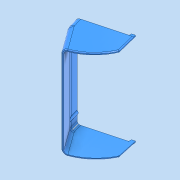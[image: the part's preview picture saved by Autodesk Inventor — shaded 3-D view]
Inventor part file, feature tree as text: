
AUTODESK INVENTOR PART (.ipt)
format: ipt  version: 2022 (Build 260153070, 153G)  size: 537,088 bytes
history: native  units: mm
features: other x16, extrude x10, sketch x9, plane x6, surface_op x4, fillet x4, split x3, thicken_offset x1, mirror x1
ambient origin geometry x8: Origin, YZ Plane, XZ Plane, XY Plane, X Axis, Y Axis, Z Axis, Center Point
bodies: Solid2 (feature_tree)
feature tree (54):
  other  "P00173-09-002.ipt"
  other  "P00173-09-003.ipt"
  other  "Blocks"
  sketch  "Sketch8"  dims[d187=8.0mm d188=24.0mm d189=25.0mm]
  sketch  "Sketch7"  dims[d31=10.0mm d40=10.0mm]
  plane  "Work Plane1"
  sketch  "Sketch5"  dims[d16=464.0mm d17=0.0mm d20=320.625mm d21=0.0mm]
  plane  "Work Plane5"
  plane  "Work Plane2"
  sketch  "Sketch15"  dims[d194=9.5mm d201=21.0mm d202=2.0mm]
  plane  "Work Plane6"
  plane  "Work Plane8"
  sketch  "Sketch21"  dims[d203=12.5mm d204=2.1mm]
  sketch  "Sketch6"  dims[d23=118.25mm d24=0.0mm d28=3.5mm d29=2.5mm]
  surface_op  "Trim15"
  surface_op  "Extend1"
  surface_op  "Trim16"
  surface_op  "Stitch Surface2"
  fillet  "Fillet14"  Radius=10.0mm
  fillet  "Fillet15"  Radius=89.5mm
  thicken_offset  "Thicken2"
  split  "Split2"
  extrude  "Extrusion4"  Depth=320.625mm TaperAngle=0.0deg
  extrude  "Extrusion13"  Depth=3.5mm
  extrude  "Extrusion14"  Depth=10.0mm
  extrude  "Extrusion5"  Depth=24.0mm
  split  "Split4"
  split  "Split6"
  fillet  "Fillet16"  Radius=25.0mm
  extrude  "Extrusion16"  Depth=2.0mm
  mirror  "Mirror3"
  fillet  "Fillet17"  Radius=2.0mm
  other  "Side"
  other  "Bottom"
  other  "Srf1"
  other  "Srf6"
  other  "Srf8"
  other  "Srf9"
  other  "Camera_Top"
  other  "Top_Housing"
  other  "Top_Housing_Bottom_Edge"
  other  "Cover_Mount"
  plane  "Work Plane - Screen_Top"
  sketch  "Sketch22"  dims[d52=15.882496mm d54=8.0mm]
  other  "Srf14"
  sketch  "Sketch23"  dims[d55=8.0mm d69=3.0mm]
  other  "Srf15"
  sketch  "Sketch25"  dims[d70=7.0mm d71=2.5mm d72=52.75mm d73=0.0mm d74=10.0mm d75=0.0mm d98=7.5mm d99=20.0mm d100=10.0mm d103=100.0mm d104=100.0mm d106=25.0mm d108=1.5mm d109=75.0deg d110=6.0mm d122=2.0mm d123=20.0mm d124=20.0mm d126=20.0mm d127=20.0mm d128=130.0mm d129=0.0mm d133=5.0mm d135=20.0mm d136=20.0mm d137=130.0mm d138=0.0mm d139=130.0mm d140=0.0mm d141=5.0mm d142=-0.349066mm d144=1.0mm d145=7.960614mm d146=0.0mm d147=65.0mm d148=0.174533mm d149=0.5mm d150=45.375mm d151=0.0mm d152=3.0mm d153=0.0mm d159=5.0mm d161=10.0mm d162=1.0mm d163=0.0mm d164=2.0mm d165=10.0mm d166=15.0mm d115=0.5mm d116=0.872665mm d117=0.5mm d118=0.872665mm]
  extrude  "ExtrusionSrf13"  Depth=2.1mm
  extrude  "ExtrusionSrf12"  Depth=8.0mm
  extrude  "ExtrusionSrf1"  Depth=3.0mm
  extrude  "ExtrusionSrf5"  Depth=10.0mm
  extrude  "ExtrusionSrf7"  Depth=10.0mm TaperAngle=0.0deg
  other  "Camera_Top:1"
